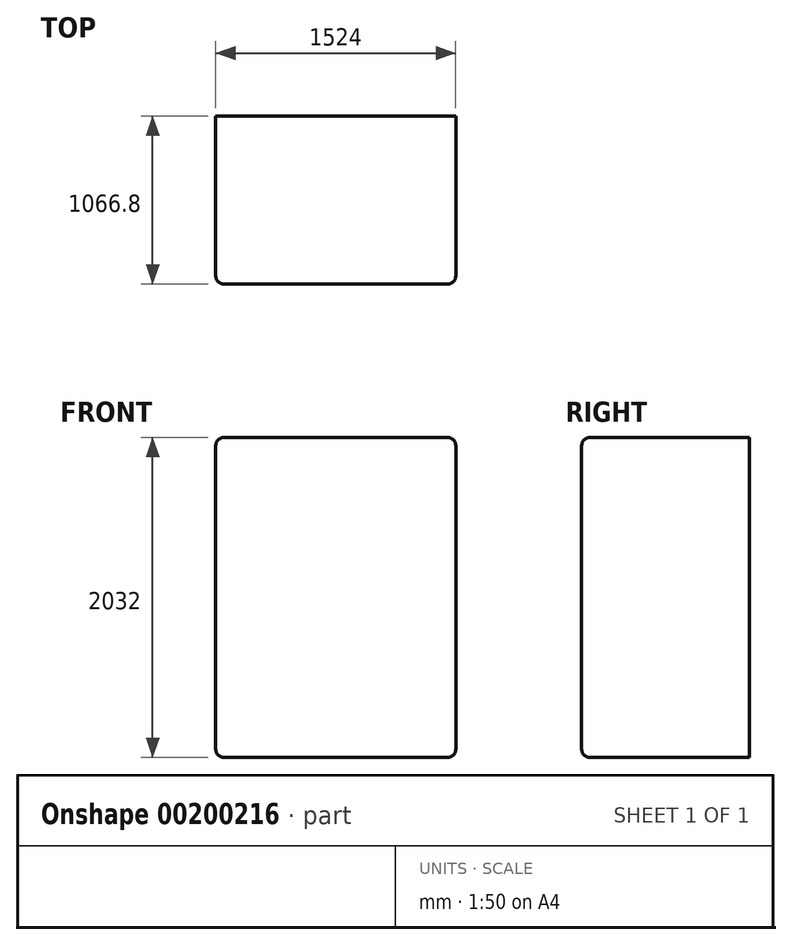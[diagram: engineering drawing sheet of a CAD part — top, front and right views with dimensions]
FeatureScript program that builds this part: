
annotation { "Feature Type Name" : "Feature", "Feature Type Description" : "" }
export const myFeature = defineFeature(function(context is Context, id is Id, definition is map)
    precondition{}
    {
        {
            var Q0;
            Q0=qCreatedBy(makeId("Front.planeOp"),FACE);
            var sketch = newSketch(context, id + "F0", { "sketchPlane" : qUnion([Q0])});
            skLineSegment(sketch, "E0.bottom", {"start": v(-41.49, 2032) * mm, "end": v(1482.51, 2032) * mm});
            skLineSegment(sketch, "E0.top", {"start": v(-41.49, 0) * mm, "end": v(1482.51, 0) * mm});
            skLineSegment(sketch, "E0.left", {"start": v(-41.49, 2032) * mm, "end": v(-41.49, 0) * mm});
            skLineSegment(sketch, "E0.right", {"start": v(1482.51, 2032) * mm, "end": v(1482.51, 0) * mm});
            skSolve(sketch);
        }
        {
            var Q0;
            Q0 = qSketchRegion(id + "F0", true);
            extrude(context, id + "F1", {"entities" : qUnion([Q0]), "depth" : 1066.8 * mm});
        }
        {
            var Q0;
            Q0=makeQuery(id+"F1.opExtrude","CAP_EDGE",EDGE,{"disambiguationData":[OSD([sQuery(id+"F0.wireOp",EDGE,"E0.left")])],"isStart":false});
            var Q1;
            Q1=makeQuery(id+"F1.opExtrude","CAP_EDGE",EDGE,{"disambiguationData":[OSD([sQuery(id+"F0.wireOp",EDGE,"E0.bottom")])],"isStart":false});
            var Q2;
            Q2=makeQuery(id+"F1.opExtrude","CAP_EDGE",EDGE,{"disambiguationData":[OSD([sQuery(id+"F0.wireOp",EDGE,"E0.right")])],"isStart":false});
            var Q3;
            Q3=makeQuery(id+"F1.opExtrude","CAP_EDGE",EDGE,{"disambiguationData":[OSD([sQuery(id+"F0.wireOp",EDGE,"E0.top")])],"isStart":false});
            var Q4;
            Q4=makeQuery(id+"F1.opExtrude","SWEPT_EDGE",EDGE,{"disambiguationData":[OSD([sQuery(id+"F0.wireOp",EDGE,"E0.top"),sQuery(id+"F0.wireOp",EDGE,"E0.left")])]});
            var Q5;
            Q5=makeQuery(id+"F1.opExtrude","SWEPT_EDGE",EDGE,{"disambiguationData":[OSD([sQuery(id+"F0.wireOp",EDGE,"E0.bottom"),sQuery(id+"F0.wireOp",EDGE,"E0.left")])]});
            var Q6;
            Q6=makeQuery(id+"F1.opExtrude","SWEPT_EDGE",EDGE,{"disambiguationData":[OSD([sQuery(id+"F0.wireOp",EDGE,"E0.bottom"),sQuery(id+"F0.wireOp",EDGE,"E0.right")])]});
            var Q7;
            Q7=makeQuery(id+"F1.opExtrude","SWEPT_EDGE",EDGE,{"disambiguationData":[OSD([sQuery(id+"F0.wireOp",EDGE,"E0.top"),sQuery(id+"F0.wireOp",EDGE,"E0.right")])]});
            fillet(context, id + "F2", {"entities" : qUnion([Q0, Q1, Q2, Q3, Q4, Q5, Q6, Q7]), "radius" : 50.8 * mm, "tangentPropagation" : true, "allowEdgeOverflow" : false});
        }
    });
